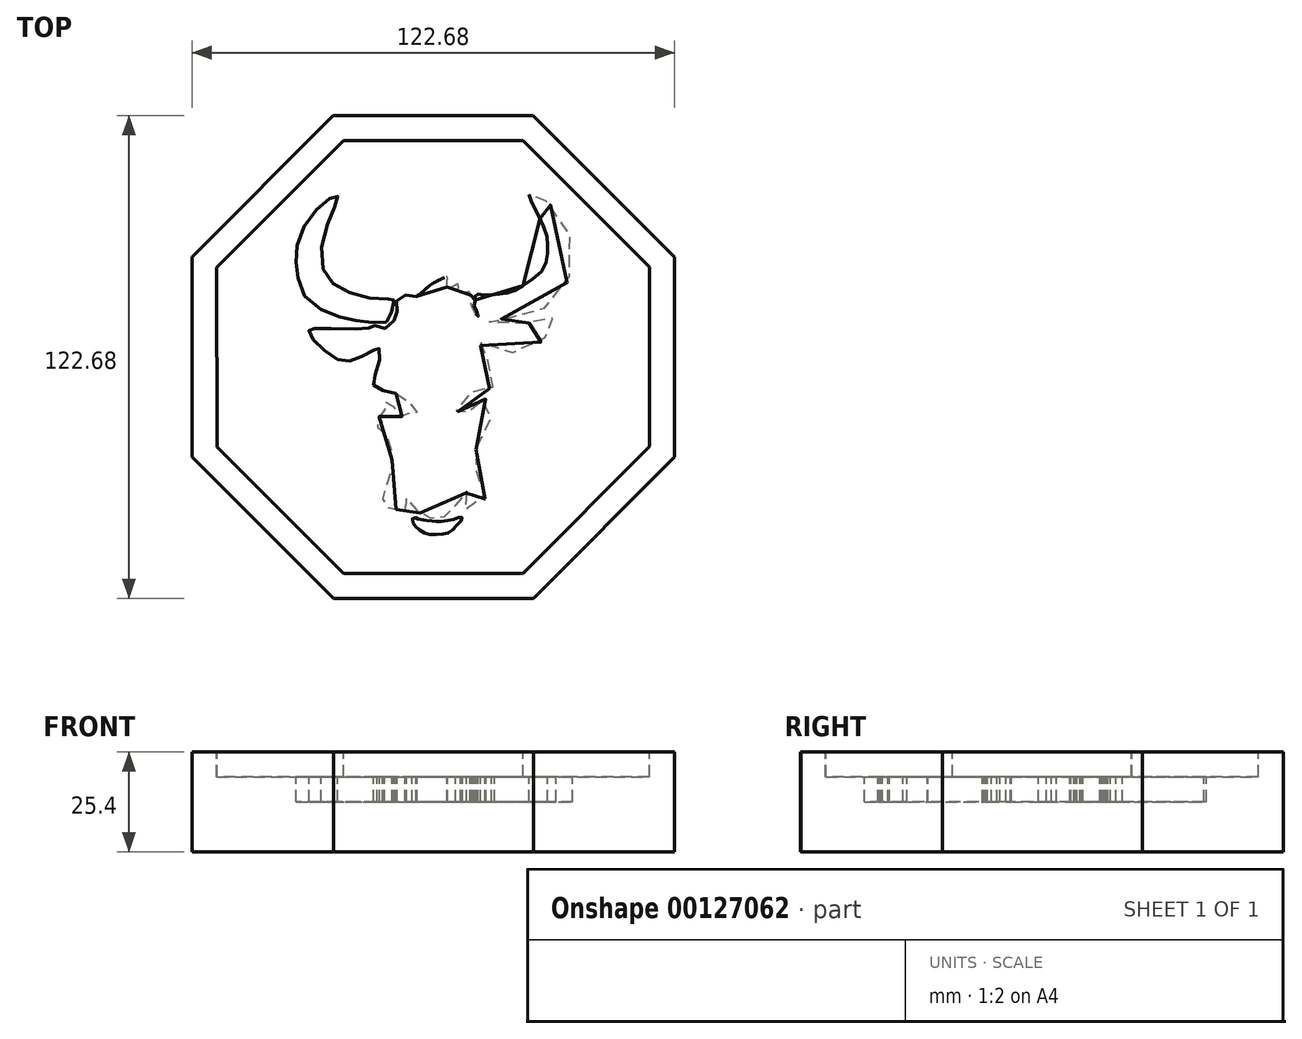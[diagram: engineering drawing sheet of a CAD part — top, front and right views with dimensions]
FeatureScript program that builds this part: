
annotation { "Feature Type Name" : "Feature", "Feature Type Description" : "" }
export const myFeature = defineFeature(function(context is Context, id is Id, definition is map)
    precondition{}
    {
        {
            var Q0;
            Q0=qCreatedBy(makeId("Top.planeOp"),FACE);
            var sketch = newSketch(context, id + "F0", { "sketchPlane" : qUnion([Q0])});
            skCircle(sketch, "E0.cCircle", {"center": v(0, 0) * mm, "radius": 61.32 * mm, "construction": true});
            skLineSegment(sketch, "E0.0", {"start": v(-61.3, -25.44) * mm, "end": v(-61.34, 25.36) * mm});
            skLineSegment(sketch, "E0.1", {"start": v(-61.34, 25.36) * mm, "end": v(-25.44, 61.3) * mm});
            skLineSegment(sketch, "E0.2", {"start": v(-25.44, 61.3) * mm, "end": v(25.36, 61.34) * mm});
            skLineSegment(sketch, "E0.3", {"start": v(25.36, 61.34) * mm, "end": v(61.3, 25.44) * mm});
            skLineSegment(sketch, "E0.4", {"start": v(61.3, 25.44) * mm, "end": v(61.34, -25.36) * mm});
            skLineSegment(sketch, "E0.5", {"start": v(61.34, -25.36) * mm, "end": v(25.44, -61.3) * mm});
            skLineSegment(sketch, "E0.6", {"start": v(25.44, -61.3) * mm, "end": v(-25.36, -61.34) * mm});
            skLineSegment(sketch, "E0.7", {"start": v(-25.36, -61.34) * mm, "end": v(-61.3, -25.44) * mm});
            skPoint(sketch, "E0.0.midPoint", {"position": v(-61.32, -0.04) * mm});
            skSolve(sketch);
        }
        {
            var Q0;
            Q0=qSketchRegion(id+"F0",true);
            extrude(context, id + "F1", {"entities" : qUnion([Q0]), "depth" : 25.4 * mm});
        }
        {
            var Q0;
            Q0=makeQuery(id+"F1.opExtrude","CAP_FACE",FACE,{"disambiguationData":[OSD([sQuery(id+"F0.wireOp",EDGE,"E0.0"),sQuery(id+"F0.wireOp",EDGE,"E0.1"),sQuery(id+"F0.wireOp",EDGE,"E0.2"),sQuery(id+"F0.wireOp",EDGE,"E0.3"),sQuery(id+"F0.wireOp",EDGE,"E0.4"),sQuery(id+"F0.wireOp",EDGE,"E0.5"),sQuery(id+"F0.wireOp",EDGE,"E0.6"),sQuery(id+"F0.wireOp",EDGE,"E0.7")])],"isStart":false});
            var sketch = newSketch(context, id + "F2", { "sketchPlane" : qUnion([Q0])});
            skLineSegment(sketch, "E1.0", {"start": v(-54.96, -22.8) * mm, "end": v(-54.99, 22.73) * mm});
            skLineSegment(sketch, "E1.1", {"start": v(-22.73, -54.99) * mm, "end": v(-54.96, -22.8) * mm});
            skLineSegment(sketch, "E1.2", {"start": v(-54.99, 22.73) * mm, "end": v(-22.8, 54.96) * mm});
            skLineSegment(sketch, "E1.3", {"start": v(22.8, -54.96) * mm, "end": v(-22.73, -54.99) * mm});
            skLineSegment(sketch, "E1.4", {"start": v(-22.8, 54.96) * mm, "end": v(22.73, 54.99) * mm});
            skLineSegment(sketch, "E1.5", {"start": v(22.73, 54.99) * mm, "end": v(54.96, 22.8) * mm});
            skLineSegment(sketch, "E1.6", {"start": v(54.96, 22.8) * mm, "end": v(54.99, -22.73) * mm});
            skLineSegment(sketch, "E1.7", {"start": v(54.99, -22.73) * mm, "end": v(22.8, -54.96) * mm});
            skSolve(sketch);
        }
        {
            var Q0;
            Q0=qSketchRegion(id+"F2",true);
            extrude(context, id + "F3", {"entities" : qUnion([Q0]), "operationType" : NewBodyOperationType.REMOVE, "oppositeDirection" : true, "depth" : 6.35 * mm});
        }
        {
            var Q0;
            Q0=makeQuery(id+"F3.boolean.opBoolean","COPY",FACE,{"derivedFrom":makeQuery(id+"F3.opExtrude","CAP_FACE",FACE,{"disambiguationData":[OSD([sQuery(id+"F2.wireOp",EDGE,"E1.0"),sQuery(id+"F2.wireOp",EDGE,"E1.1"),sQuery(id+"F2.wireOp",EDGE,"E1.2"),sQuery(id+"F2.wireOp",EDGE,"E1.3"),sQuery(id+"F2.wireOp",EDGE,"E1.4"),sQuery(id+"F2.wireOp",EDGE,"E1.5"),sQuery(id+"F2.wireOp",EDGE,"E1.6"),sQuery(id+"F2.wireOp",EDGE,"E1.7")])],"isStart":false})});
            var sketch = newSketch(context, id + "F4", { "sketchPlane" : qUnion([Q0])});
            skFitSpline(sketch, "E2", {"points": [v(-11.93, 8.9) * mm, v(-10.74, 10.9) * mm, v(-10.14, 13.36) * mm, v(-10.07, 15.02) * mm, v(-10.74, 14.9) * mm, v(-16.12, 14.96) * mm, v(-23.03, 17.22) * mm, v(-27.35, 20.87) * mm, v(-28.22, 28.72) * mm, v(-25.56, 37.02) * mm, v(-24.43, 39.88) * mm, v(-24.43, 41.01) * mm, v(-25.82, 40.61) * mm, v(-29.61, 37.62) * mm, v(-33.87, 30.98) * mm, v(-34.86, 24.93) * mm, v(-34.53, 20.67) * mm, v(-32.07, 14.76) * mm, v(-25.03, 10.64) * mm, v(-20.1, 9.37) * mm, v(-15.19, 8.78) * mm, v(-11.93, 8.9) * mm]});
            skFitSpline(sketch, "E3", {"points": [v(-4.44, 15.33) * mm, v(-5.94, 15.53) * mm, v(-8.16, 15.57) * mm, v(-9.42, 14.06) * mm, v(-9.26, 12.2) * mm, v(-9.3, 10.94) * mm, v(-9.82, 9.6) * mm, v(-11.56, 7.5) * mm, v(-13.37, 7.35) * mm, v(-14.76, 7.98) * mm, v(-15.59, 7.9) * mm, v(-16.38, 7.42) * mm, v(-16.7, 7.19) * mm, v(-23.14, 7.23) * mm, v(-29.62, 7.23) * mm, v(-30.96, 7.35) * mm, v(-31.4, 7.23) * mm, v(-31.55, 6.16) * mm, v(-30.8, 4.82) * mm, v(-28.31, 2.25) * mm, v(-24.68, -0.48) * mm, v(-22.42, -0.87) * mm, v(-20.17, -0.87) * mm, v(-17.33, 0.7) * mm, v(-14.84, 1.9) * mm, v(-14.28, 2.33) * mm, v(-13.85, 2.29) * mm, v(-13.69, 1.38) * mm, v(-13.77, -1.5) * mm, v(-14.91, -5.07) * mm, v(-15.23, -6.38) * mm, v(-14.68, -7.86) * mm, v(-12.25, -8.65) * mm, v(-9.43, -9.23) * mm], "startDerivative": vector(-52.24, 5.79) * mm, "endDerivative": vector(74.94, -16.57) * mm});
            skFitSpline(sketch, "E4", {"points": [v(-9.43, -9.23) * mm, v(-6.61, -11.14) * mm, v(-4.45, -13.23) * mm, v(-4.19, -14.2) * mm, v(-4.85, -14.73) * mm, v(-6.02, -14.4) * mm, v(-6.91, -14.93) * mm, v(-8.3, -15.1) * mm, v(-9.43, -13.83) * mm, v(-10.17, -12.37) * mm, v(-10.74, -11.67) * mm, v(-12.4, -11.7) * mm, v(-12.46, -12.63) * mm, v(-12.46, -13.57) * mm, v(-13.53, -14.83) * mm, v(-14.26, -16.06) * mm, v(-14.32, -16.79) * mm, v(-14.16, -17.79) * mm, v(-13.2, -18.65) * mm, v(-11.73, -20.11) * mm, v(-10.74, -23.34) * mm, v(-10.53, -28.35) * mm, v(-11.87, -32.59) * mm, v(-12.72, -34.38) * mm, v(-12.82, -37.12) * mm, v(-12.22, -37.96) * mm, v(-8.13, -38.96) * mm, v(-6.99, -39.16) * mm, v(-6.84, -38.26) * mm, v(-6.9, -35.92) * mm, v(-7.14, -35.33) * mm, v(-6.44, -36.27) * mm, v(-4.3, -38.86) * mm, v(-1.36, -40.7) * mm, v(1.57, -41.1) * mm, v(3.97, -39.46) * mm, v(6.45, -36.82) * mm, v(8.2, -34.83) * mm, v(8.45, -34.38) * mm, v(8.3, -35.08) * mm, v(7.6, -37.27) * mm, v(6.95, -38.61) * mm, v(9, -38.61) * mm, v(12.08, -37.62) * mm, v(13.13, -36.02) * mm, v(12.33, -33.53) * mm, v(10.79, -32.34) * mm, v(10.99, -29) * mm, v(10.14, -29.15) * mm, v(10.64, -24.52) * mm, v(11.43, -21.98) * mm, v(13.43, -19) * mm, v(14.57, -16.4) * mm, v(14.62, -12.12) * mm, v(13.82, -10.78) * mm, v(12.88, -10.83) * mm, v(11.53, -12.02) * mm, v(10.89, -13.12) * mm, v(10.09, -13.96) * mm, v(8.9, -14.06) * mm, v(8.5, -13.12) * mm, v(7.6, -12.97) * mm, v(6.5, -13.62) * mm, v(6.06, -13.86) * mm, v(5.7, -13.57) * mm, v(6.26, -12.12) * mm, v(7.95, -10.03) * mm, v(11.14, -8.24) * mm, v(12.48, -7.79) * mm, v(13.53, -7.99) * mm, v(15.22, -7.5) * mm, v(15.17, -4.05) * mm, v(14.48, -2.23) * mm, v(13.56, -0.5) * mm, v(12.41, 0.5) * mm, v(12.08, 1.78) * mm, v(12.13, 3.62) * mm, v(12.39, 3.4) * mm, v(16.2, 1.97) * mm, v(21.15, 1.15) * mm, v(25.8, 2.58) * mm, v(29.32, 5.92) * mm, v(31.1, 8.47) * mm, v(31.04, 9.6) * mm, v(30.2, 9.83) * mm, v(28.55, 9.24) * mm, v(24.64, 8.64) * mm, v(19.6, 8.76) * mm, v(15.88, 8.82) * mm, v(13.57, 9.12) * mm, v(13.63, 9.77) * mm, v(16.12, 9.65) * mm, v(21.03, 10.42) * mm, v(25.95, 11.6) * mm, v(30.74, 14.03) * mm, v(34.18, 19.3) * mm, v(35.36, 24.28) * mm, v(34.6, 31.38) * mm, v(30.92, 37.3) * mm, v(27.87, 40.39) * mm, v(26.36, 41.42) * mm, v(25.33, 41.7) * mm, v(24.39, 41.6) * mm, v(24.76, 39.92) * mm, v(26.55, 36.34) * mm, v(28.8, 30.8) * mm, v(29, 27.04) * mm, v(28.05, 22.53) * mm, v(22.66, 18.1) * mm, v(19.07, 16.3) * mm, v(15.59, 15.9) * mm, v(12.55, 15.7) * mm, v(11.1, 15.96) * mm, v(10.6, 15.36) * mm, v(10.66, 13.82) * mm, v(10.4, 13.07) * mm, v(11.06, 11.48) * mm, v(11.35, 10.33) * mm, v(10.6, 11.13) * mm, v(9.76, 13.02) * mm, v(9.41, 14.12) * mm, v(9.41, 16) * mm, v(9.06, 16.66) * mm, v(8.47, 16.46) * mm, v(6.92, 16.56) * mm, v(6.52, 17) * mm, v(6.13, 18.7) * mm, v(5.88, 18.4) * mm, v(4.38, 17.6) * mm, v(3.64, 17.3) * mm, v(3.54, 18.3) * mm, v(3.59, 19.7) * mm, v(3.59, 20.4) * mm, v(2.54, 20.04) * mm, v(-0.8, 18.3) * mm, v(-2.49, 16.7) * mm, v(-4.44, 15.33) * mm], "startDerivative": vector(301.7, -189.61) * mm, "endDerivative": vector(-265.9, -165.89) * mm});
            skFitSpline(sketch, "E5", {"points": [v(-0.27, -41.62) * mm, v(-1.86, -41.52) * mm, v(-2.4, -41.42) * mm, v(-3.9, -41.09) * mm, v(-4.2, -40.92) * mm, v(-4.95, -40.79) * mm, v(-5.39, -41.42) * mm, v(-5.05, -42.35) * mm, v(-4.2, -43.41) * mm, v(-2.73, -44.48) * mm, v(-1.2, -45.04) * mm, v(1.36, -45.04) * mm, v(3.42, -44.88) * mm, v(4.85, -43.98) * mm, v(6.24, -42.42) * mm, v(7.37, -41.15) * mm, v(7.04, -40.59) * mm, v(6.21, -40.85) * mm, v(4.55, -41.42) * mm, v(2.22, -41.72) * mm, v(0.63, -41.72) * mm, v(-0.27, -41.62) * mm]});
            skSolve(sketch);
        }
        {
            var Q0;
            Q0=makeQuery(id+"F4.imprint","IMPRINT",FACE,{"disambiguationData":[TD([[makeQuery(id+"F4.imprint","IMPRINT",EDGE,{"derivedFrom":sQuery(id+"F4.wireOp",EDGE,"E3")}),1.0]])]});
            var Q1;
            Q1=makeQuery(id+"F4.imprint","IMPRINT",FACE,{"disambiguationData":[TD([[makeQuery(id+"F4.imprint","IMPRINT",EDGE,{"derivedFrom":sQuery(id+"F4.wireOp",EDGE,"E2")}),1.0]])]});
            var Q2;
            Q2=makeQuery(id+"F4.imprint","IMPRINT",FACE,{"disambiguationData":[TD([[makeQuery(id+"F4.imprint","IMPRINT",EDGE,{"derivedFrom":sQuery(id+"F4.wireOp",EDGE,"E5")}),1.0]])]});
            extrude(context, id + "F5", {"entities" : qUnion([Q0, Q1, Q2]), "operationType" : NewBodyOperationType.REMOVE, "oppositeDirection" : true, "depth" : 6.35 * mm});
        }
    });
